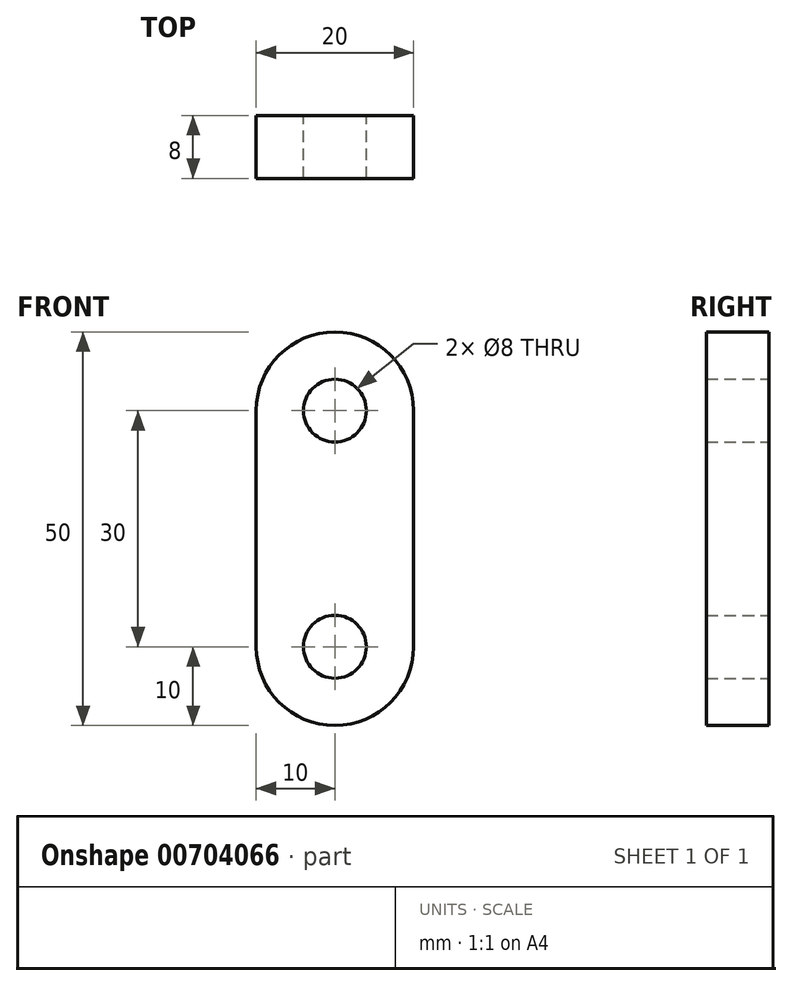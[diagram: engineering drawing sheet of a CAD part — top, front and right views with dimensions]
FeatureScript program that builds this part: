
annotation { "Feature Type Name" : "Feature", "Feature Type Description" : "" }
export const myFeature = defineFeature(function(context is Context, id is Id, definition is map)
    precondition{}
    {
        {
            var Q0;
            Q0=qCreatedBy(makeId("Front.planeOp"),FACE);
            var sketch = newSketch(context, id + "F0", { "sketchPlane" : qUnion([Q0])});
            skCircle(sketch, "E0", {"center": v(0, 0) * mm, "radius": 4 * mm});
            skArc(sketch, "E1", {"start": v(-10, 0) * mm, "mid": v(0, -10) * mm, "end": v(10, 0) * mm});
            skCircle(sketch, "E2", {"center": v(0, 30) * mm, "radius": 4 * mm});
            skArc(sketch, "E3", {"start": v(10, 30) * mm, "mid": v(0, 40) * mm, "end": v(-10, 30) * mm});
            skLineSegment(sketch, "E4", {"start": v(-10, 30) * mm, "end": v(-10, 0) * mm});
            skLineSegment(sketch, "E5", {"start": v(10, 30) * mm, "end": v(10, 0) * mm});
            skSolve(sketch);
        }
        {
            var Q0;
            Q0=makeQuery(id+"F0.imprint","IMPRINT",FACE,{"disambiguationData":[TD([[makeQuery(id+"F0.imprint","IMPRINT",EDGE,{"derivedFrom":sQuery(id+"F0.wireOp",EDGE,"E0")}),-1.0]])]});
            extrude(context, id + "F1", {"entities" : qUnion([Q0]), "depth" : 8 * mm, "offsetDistance" : 25.4 * mm});
        }
    });
